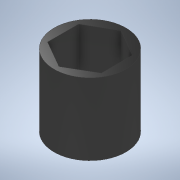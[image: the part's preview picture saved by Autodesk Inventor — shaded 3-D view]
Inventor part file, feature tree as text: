
AUTODESK INVENTOR PART (.ipt)
format: ipt  version: 2020 (Build 240168000, 168)  size: 102,912 bytes
history: native  units: in
note: dims shown in document units (in); Inventor stores cm internally (conversion verified against a paired STEP export)
features: extrude x1, sketch x1
ambient origin geometry x8: Origin, YZ Plane, XZ Plane, XY Plane, X Axis, Y Axis, Z Axis, Center Point
bodies: Solid1 (feature_tree)
feature tree (2):
  extrude  "Extrusion1"  Depth=0.5in
  sketch  "Sketch1"  dims[d0=0.375in d1=0.5in d2=0.5in d3=0.0in]
